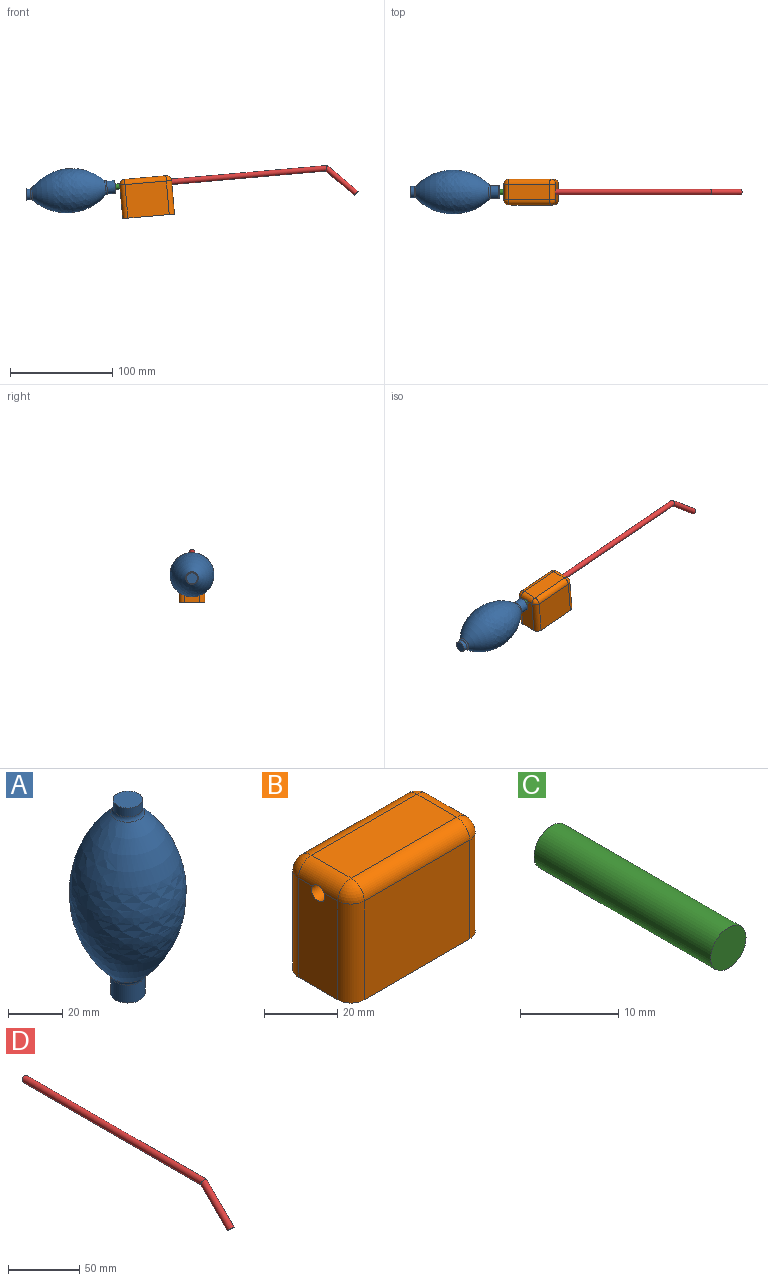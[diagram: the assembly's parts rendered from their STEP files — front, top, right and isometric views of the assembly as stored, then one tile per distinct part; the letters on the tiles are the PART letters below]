
ASSEMBLY  parts=4 mates=3
PART A: 9 faces, bbox 43.2x43.2x87.4 mm
  f0: plane 12.7x12.7mm, normal (0,0,-1), area 102.2mm2, adj f4,f5
  f1: plane 10.92x10.92mm, normal (0,0,1), area 93.7mm2, adj f2
  f2: cylinder r=5.46mm len=10.92mm, axis (0,0,-1), area 136.9mm2, adj f1,f7
  f3: revolved ~71.69x43.17mm, area 8267mm2, adj f7,f8
  f4: cylinder r=6.35mm len=12.7mm, axis (0,0,-1), area 322.7mm2, adj f0,f8
  f5: cylinder r=2.79mm len=25.4mm, axis (0,0,-1), area 445.9mm2, adj f0,f6
  f6: plane 5.59x5.59mm, normal (0,0,-1), area 24.5mm2, adj f5
  f7: torus R=8mm, axis (0,0,-1), area 73.2mm2, adj f2,f3
  f8: torus R=8.89mm, axis (0,0,-1), area 81.9mm2, adj f3,f4
PART B: 21 faces, bbox 50.8x25.4x38.1 mm
  f0: plane 40.64x15.24mm, normal (0,0,1), area 619.4mm2, adj f9,f10,f11,f12
  f1: plane 33.02x15.24mm, normal (-1,0,0), area 486.9mm2, adj f2,f8,f12,f17,f19
  f2: plane 50.8x25.4mm, normal (0,0,-1), area 1268.2mm2, adj f1,f3,f4,f5,f13,f15,f17,f19
  f3: plane 33.02x15.24mm, normal (1,0,0), area 479.5mm2, adj f2,f6,f9,f13,f15
  f4: plane 40.64x33.02mm, normal (0,-1,0), area 1341.9mm2, adj f2,f10,f13,f17
  f5: plane 40.64x33.02mm, normal (0,1,0), area 1341.9mm2, adj f2,f11,f15,f19
  f6: cylinder r=3.17mm len=25.4mm, axis (1,0,0), area 505.3mm2, adj f3,f7,f9
  f7: plane 6.35x6.35mm, normal (1,0,0), area 11.4mm2, adj f6,f8
  f8: cylinder r=2.54mm len=25.4mm, axis (-1,0,0), area 404.9mm2, adj f1,f7,f12
  f9: cylinder r=5.08mm len=15.24mm, axis (0,1,0), area 113.5mm2, adj f0,f3,f6,f14,f16
  f10: cylinder r=5.08mm len=40.64mm, axis (1,0,0), area 324.3mm2, adj f0,f4,f14,f18
  f11: cylinder r=5.08mm len=40.64mm, axis (-1,0,0), area 324.3mm2, adj f0,f5,f16,f20
  f12: cylinder r=5.08mm len=15.24mm, axis (0,-1,0), area 117.6mm2, adj f0,f1,f8,f18,f20
  f13: cylinder r=5.08mm len=33.02mm, axis (0,0,-1), area 263.5mm2, adj f2,f3,f4,f14
  f14: sphere r=5.08mm, area 40.5mm2, adj f9,f10,f13
  f15: cylinder r=5.08mm len=33.02mm, axis (0,0,1), area 263.5mm2, adj f2,f3,f5,f16
  f16: sphere r=5.08mm, area 40.5mm2, adj f9,f11,f15
  f17: cylinder r=5.08mm len=33.02mm, axis (0,0,1), area 263.5mm2, adj f1,f2,f4,f18
  f18: sphere r=5.08mm, area 40.5mm2, adj f10,f12,f17
  f19: cylinder r=5.08mm len=33.02mm, axis (0,0,-1), area 263.5mm2, adj f1,f2,f5,f20
  f20: sphere r=5.08mm, area 40.5mm2, adj f11,f12,f19
PART C: 3 faces, bbox 5.1x25.4x5.1 mm
  f0: cylinder r=2.54mm len=25.4mm, axis (0,1,0), area 405.4mm2, adj f1,f2
  f1: plane 5.08x5.08mm, normal (0,-1,0), area 20.3mm2, adj f0
  f2: plane 5.08x5.08mm, normal (0,1,0), area 20.3mm2, adj f0
PART D: 4 faces, bbox 5.3x206.6x31.5 mm
  f0: plane 5.33x3.77mm, normal (0,-0.71,-0.71), area 22.3mm2, adj f2
  f1: plane 5.33x5.33mm, normal (0,1,0), area 22.3mm2, adj f3
  f2: cylinder r=2.67mm len=31.49mm, axis (0,-0.71,-0.71), area 638.5mm2, adj f0,f3
  f3: cylinder r=2.67mm len=178.9mm, axis (0,-1,0), area 2979.4mm2, adj f1,f2
PLACE A rot(axis=(0,-1,0),95deg) t=(-18.6,0,32.98)mm
PLACE B rot(axis=(0,-1,0),5deg) t=(13.21,0,13.76)mm
PLACE C rot(axis=(-0.54,-0.59,-0.59),122.9deg) t=(-0.55,0,25.31)mm
PLACE D rot(axis=(-0.04,-0.04,1),90.1deg) t=(12.1,0,26.42)mm
MATE fastened C.f0 <-> A.f2  axis (-1,0,-0.09) through (-25.85,0,23.1)mm
MATE fastened C.f0 <-> B.f6  axis (1,0,0.09) through (-0.55,0,25.31)mm
MATE fastened D.f3 <-> B.f6  axis (-1,0,-0.09) through (12.1,0,26.42)mm
